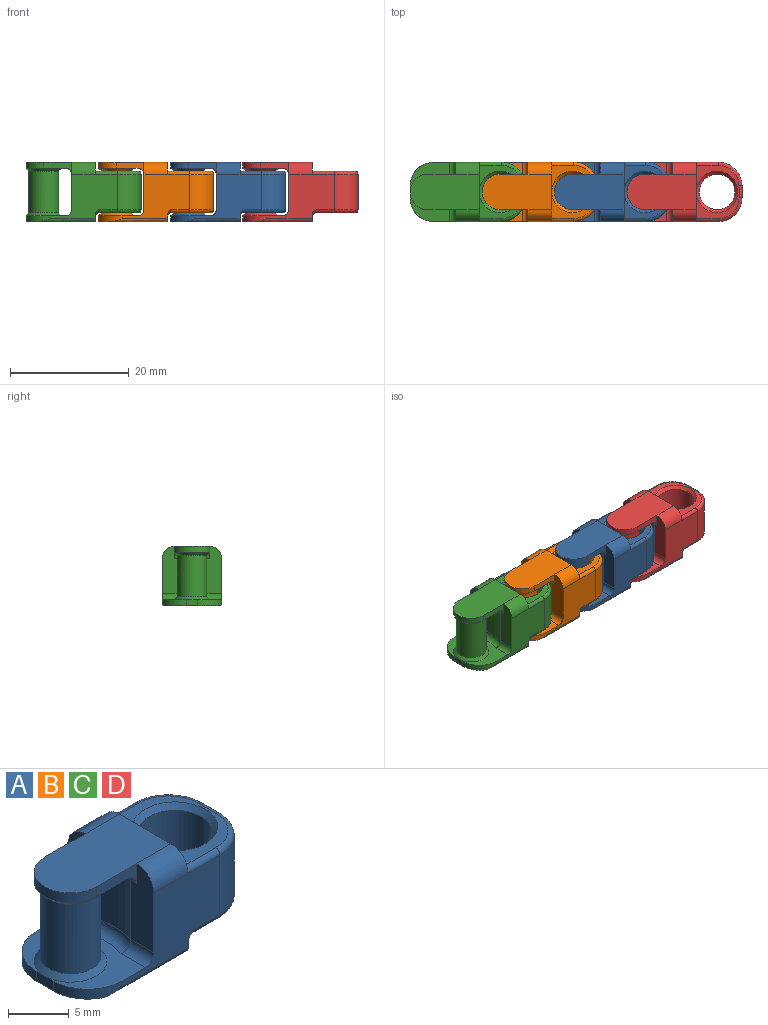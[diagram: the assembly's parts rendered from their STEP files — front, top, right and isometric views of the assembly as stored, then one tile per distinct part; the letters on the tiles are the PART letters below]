
ASSEMBLY  parts=4 mates=9
PART A: 59 faces, bbox 19.9x11.7x10.2 mm
  f0: plane 11.7x9mm, normal (0,0,-1), area 94.5mm2, adj f1,f3,f4,f12,f22,f38,f39,f40
  f1: plane 1.13x0.8mm, normal (1,0,0), area 0.8mm2, adj f0,f9,f38,f41,f42,f58
  f2: plane 11.59x7.69mm, normal (0,-1,0), area 54.4mm2, adj f3,f5,f11,f21,f22,f26,f31,f43
  f3: plane 1.13x0.8mm, normal (1,0,0), area 0.8mm2, adj f0,f2,f40,f43,f45,f57
  f4: cylinder r=4mm len=4mm, axis (0,0,-1), area 5.8mm2, adj f0,f9,f11,f12,f58
  f5: plane 8x2.66mm, normal (-1,0,0), area 19.1mm2, adj f2,f23,f48,f49,f52,f56
  f6: plane 8x2.66mm, normal (-1,0,0), area 19.1mm2, adj f9,f25,f48,f51,f54,f55
  f7: plane 11.7x6mm, normal (0,0,1), area 66.3mm2, adj f10,f23,f24,f25,f55,f56
  f8: plane 6x4.05mm, normal (0,0,-1), area 9.1mm2, adj f17,f23,f25,f49,f50,f51
  f9: plane 11.59x7.69mm, normal (0,1,0), area 54.4mm2, adj f1,f4,f6,f11,f20,f30,f35,f41
  f10: plane 10x2mm, normal (1,0,0), area 13.4mm2, adj f7,f15,f31,f35,f55,f56
  f11: plane 10x7.05mm, normal (0,0,1), area 32.9mm2, adj f2,f4,f9,f12,f18,f22,f52,f53
  f12: plane 2x1mm, normal (-1,0,0), area 2mm2, adj f0,f4,f11,f22
  f13: plane 9x7.6mm, normal (0,0,-1), area 22.9mm2, adj f26,f27,f28,f29,f30,f36,f42,f44
  f14: plane 6x2mm, normal (1,0,0), area 12mm2, adj f20,f21,f28,f33
  f15: plane 9x7.2mm, normal (0,0,1), area 21.1mm2, adj f10,f31,f32,f33,f34,f35,f37
  f16: cylinder r=2.5mm len=7mm, axis (0,0,-1), area 110mm2, adj f17,f18
  f17: cone r=3mm half-angle=45deg, axis (0,0,1), area 12.2mm2, adj f8,f16,f24
  f18: cone r=3mm half-angle=45deg, axis (0,0,-1), area 12.2mm2, adj f11,f16
  f19: cylinder r=3mm len=6mm, axis (0,0,-1), area 113.1mm2, adj f36,f37
  f20: cylinder r=4mm len=6mm, axis (0,0,1), area 37.7mm2, adj f9,f14,f29,f34
  f21: cylinder r=4mm len=6mm, axis (0,0,-1), area 37.7mm2, adj f2,f14,f27,f32
  f22: cylinder r=4mm len=4mm, axis (0,0,1), area 5.8mm2, adj f0,f2,f11,f12,f57
  f23: plane 4.7x2mm, normal (0,-1,0), area 4.9mm2, adj f5,f7,f8,f24,f49
  f24: cylinder r=3mm len=6mm, axis (0,0,-1), area 9.4mm2, adj f7,f17,f23,f25
  f25: plane 4.7x2mm, normal (0,1,0), area 4.9mm2, adj f6,f7,f8,f24,f51
  f26: cylinder r=0.5mm len=3.2mm, axis (-1,0,0), area 2.5mm2, adj f2,f13,f27,f43
  f27: torus R=3.5mm, axis (0,0,1), area 4.7mm2, adj f13,f21,f26,f28
  f28: cylinder r=0.5mm len=2mm, axis (0,1,0), area 1.6mm2, adj f13,f14,f27,f29
  f29: torus R=3.5mm, axis (0,0,1), area 4.7mm2, adj f13,f20,f28,f30
  f30: cylinder r=0.5mm len=3.2mm, axis (1,0,0), area 2.5mm2, adj f9,f13,f29,f41
  f31: cylinder r=0.5mm len=3.7mm, axis (1,0,0), area 2.9mm2, adj f2,f10,f15,f32
  f32: torus R=3.5mm, axis (0,0,-1), area 4.7mm2, adj f15,f21,f31,f33
  f33: cylinder r=0.5mm len=2mm, axis (0,1,0), area 1.6mm2, adj f14,f15,f32,f34
  f34: torus R=3.5mm, axis (0,0,-1), area 4.7mm2, adj f15,f20,f33,f35
  f35: cylinder r=0.5mm len=3.7mm, axis (-1,0,0), area 2.9mm2, adj f9,f10,f15,f34
  f36: cone r=3.5mm half-angle=45deg, axis (0,0,-1), area 14.4mm2, adj f13,f19
  f37: cone r=3.5mm half-angle=45deg, axis (0,0,1), area 14.4mm2, adj f15,f19
  f38: cylinder r=2mm len=1.67mm, axis (0,0,1), area 2mm2, adj f0,f1,f39,f44
  f39: plane 5.06x1mm, normal (1,0,0), area 5.1mm2, adj f0,f38,f40,f46
  f40: cylinder r=2mm len=1.67mm, axis (0,0,1), area 2mm2, adj f0,f3,f39,f47
  f41: torus R=1mm, axis (-1,0,0), area 0.5mm2, adj f1,f9,f30,f42
  f42: cylinder r=0.5mm len=0.6mm, axis (0,-1,0), area 0.4mm2, adj f1,f13,f41,f44
  f43: torus R=1mm, axis (-1,0,0), area 0.5mm2, adj f2,f3,f26,f45
  f44: torus R=1.5mm, axis (0,0,1), area 1.5mm2, adj f13,f38,f42,f46
  f45: cylinder r=0.5mm len=0.6mm, axis (0,-1,0), area 0.4mm2, adj f3,f13,f43,f47
  f46: cylinder r=0.5mm len=5.06mm, axis (0,-1,0), area 4mm2, adj f13,f39,f44,f47
  f47: torus R=1.5mm, axis (0,0,1), area 1.5mm2, adj f13,f40,f45,f46
  f48: cylinder r=8mm len=6mm, axis (0,0,-1), area 28.5mm2, adj f5,f6,f50,f53
  f49: cylinder r=1mm len=1mm, axis (0,-1,0), area 1.2mm2, adj f5,f8,f23,f50
  f50: torus R=7mm, axis (0,0,1), area 7.4mm2, adj f8,f48,f49,f51
  f51: cylinder r=1mm len=1mm, axis (0,-1,0), area 1.2mm2, adj f6,f8,f25,f50
  f52: cylinder r=1mm len=2.81mm, axis (0,-1,0), area 4.3mm2, adj f2,f5,f11,f53
  f53: torus R=7mm, axis (0,0,-1), area 7.4mm2, adj f11,f48,f52,f54
  f54: cylinder r=1mm len=2.81mm, axis (0,-1,0), area 4.3mm2, adj f6,f9,f11,f53
  f55: cylinder r=2mm len=4mm, axis (-1,0,0), area 12.6mm2, adj f6,f7,f9,f10
  f56: cylinder r=2mm len=4mm, axis (1,0,0), area 12.6mm2, adj f2,f5,f7,f10
  f57: cylinder r=0.5mm len=9.64mm, axis (-1,0,0), area 6.8mm2, adj f0,f2,f3,f22
  f58: cylinder r=0.5mm len=9.64mm, axis (-1,0,0), area 6.8mm2, adj f0,f1,f4,f9
PART B: same geometry as A
PART C: same geometry as A
PART D: same geometry as A
PLACE A t=(24.4,0,0)mm
PLACE B t=(12.2,0,0)mm
PLACE C at identity fixed
PLACE D t=(36.6,0,0)mm
MATE cylindrical D.f16 <-> A.f19  axis (0,0,-1) through (31.9,0,-3.5)mm
MATE planar C.f2 <-> B.f2  axis (0,-1,0) through (5.85,-5,3)mm
MATE planar A.f15 <-> D.f15  axis (0,0,1) through (31.48,0,3.5)mm
MATE planar B.f8 <-> C.f8  axis (0,0,-1) through (11.2,-2.19,4)mm
MATE planar C.f2 <-> D.f2  axis (0,-1,0) through (6.1,-5,-3)mm
MATE planar A.f8 <-> B.f8  axis (0,0,-1) through (23.4,-2.19,4)mm
MATE planar C.f2 <-> A.f2  axis (0,-1,0) through (3.44,-5,-0.58)mm
MATE cylindrical A.f16 <-> B.f19  axis (0,0,-1) through (19.7,0,-3.5)mm
MATE cylindrical B.f16 <-> C.f19  axis (0,0,-1) through (7.5,0,0)mm
